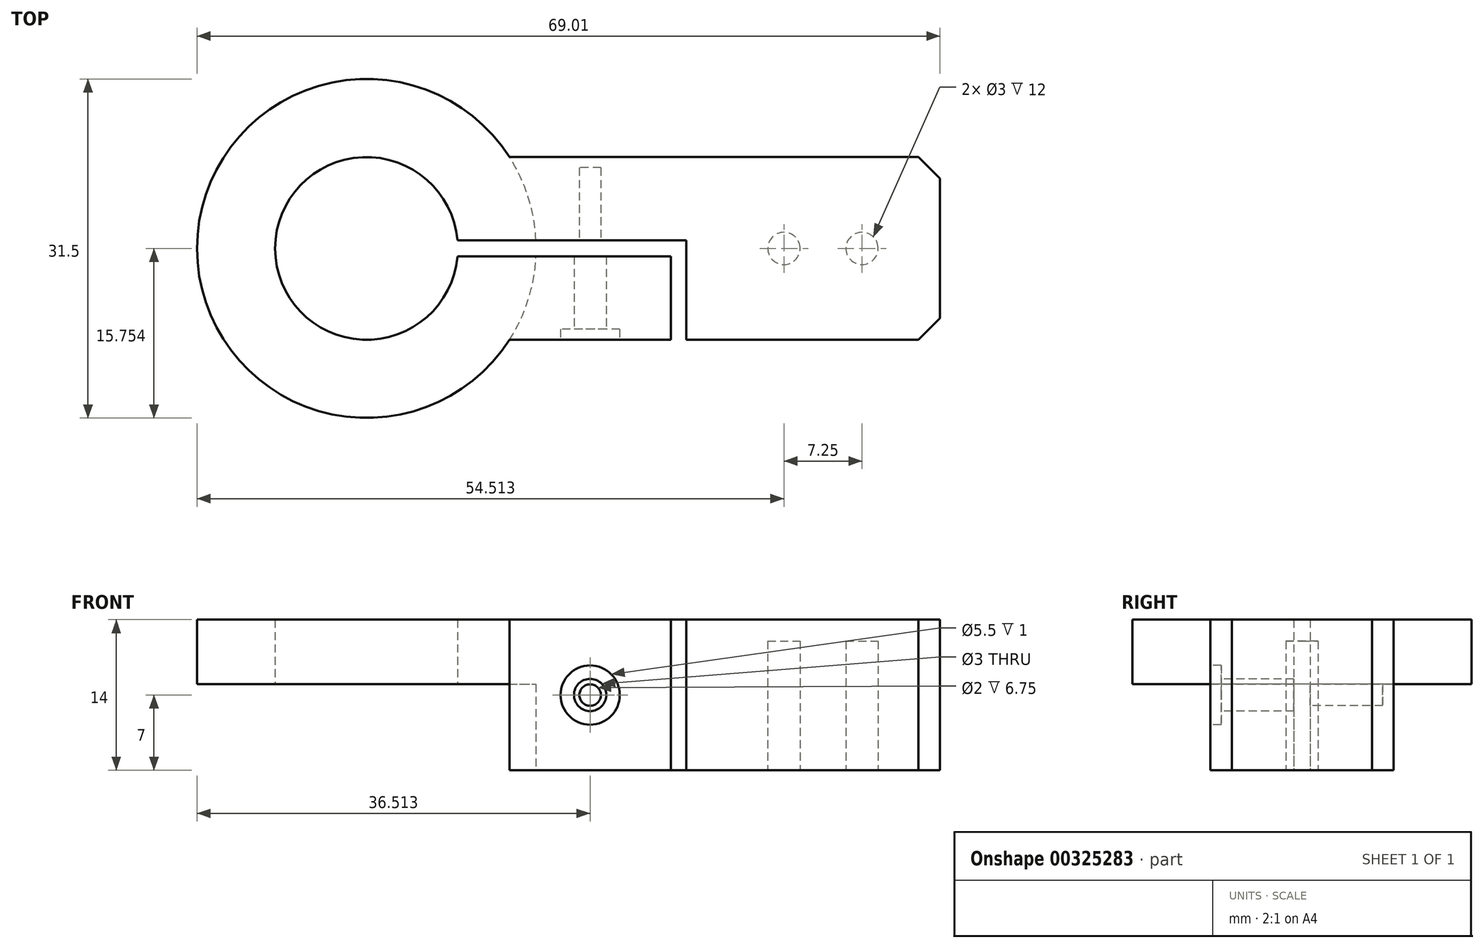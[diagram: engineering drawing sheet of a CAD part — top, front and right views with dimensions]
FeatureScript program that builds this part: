
annotation { "Feature Type Name" : "Feature", "Feature Type Description" : "" }
export const myFeature = defineFeature(function(context is Context, id is Id, definition is map)
    precondition{}
    {
        {
            var Q0;
            Q0=qCreatedBy(makeId("Top.planeOp"),FACE);
            var sketch = newSketch(context, id + "F0", { "sketchPlane" : qUnion([Q0])});
            skLineSegment(sketch, "E0.bottom", {"start": v(-112.4, -4.12) * mm, "end": v(-72.4, -4.12) * mm});
            skLineSegment(sketch, "E0.right", {"start": v(-72.4, -4.12) * mm, "end": v(-72.4, -21.12) * mm});
            skPoint(sketch, "E1", {"position": v(-141.4, -12.62) * mm});
            skArc(sketch, "E2", {"start": v(-112.4, -4.12) * mm, "mid": v(-141.4, -12.62) * mm, "end": v(-112.4, -21.12) * mm});
            skPoint(sketch, "E3", {"position": v(-134.16, -12.62) * mm});
            skPoint(sketch, "E4", {"position": v(-117.22, -13.37) * mm});
            skPoint(sketch, "E5", {"position": v(-117.22, -11.87) * mm});
            skLineSegment(sketch, "E6", {"start": v(-117.22, -13.37) * mm, "end": v(-97.4, -13.37) * mm});
            skLineSegment(sketch, "E7", {"start": v(-97.4, -13.37) * mm, "end": v(-97.4, -21.12) * mm});
            skLineSegment(sketch, "E8", {"start": v(-117.22, -11.87) * mm, "end": v(-95.97, -11.87) * mm});
            skArc(sketch, "E9", {"start": v(-117.22, -11.87) * mm, "mid": v(-134.16, -12.62) * mm, "end": v(-117.22, -13.37) * mm});
            skLineSegment(sketch, "E10", {"start": v(-95.97, -11.87) * mm, "end": v(-95.97, -21.12) * mm});
            skLineSegment(sketch, "E11", {"start": v(-95.97, -21.12) * mm, "end": v(-72.4, -21.12) * mm});
            skLineSegment(sketch, "E12", {"start": v(-112.4, -21.12) * mm, "end": v(-97.4, -21.12) * mm});
            skSolve(sketch);
        }
        {
            var Q0;
            Q0=makeQuery(id+"F0.imprint","IMPRINT",FACE,{"disambiguationData":[TD([[makeQuery(id+"F0.imprint","IMPRINT",EDGE,{"derivedFrom":sQuery(id+"F0.wireOp",EDGE,"E0.bottom")}),-1.0]])]});
            extrude(context, id + "F1", {"entities" : qUnion([Q0]), "depth" : 14 * mm});
        }
        {
            var Q0;
            Q0=makeQuery(id+"F1.opExtrude","SWEPT_FACE",FACE,{"disambiguationData":[OSD([sQuery(id+"F0.wireOp",EDGE,"E12")])]});
            var sketch = newSketch(context, id + "F2", { "sketchPlane" : qUnion([Q0])});
            skCircle(sketch, "E13", {"center": v(-104.9, 7) * mm, "radius": 2.75 * mm});
            skPoint(sketch, "E13.centerSnap0", {"position": v(-97.4, 7) * mm});
            skPoint(sketch, "E13.centerSnap1", {"position": v(-104.9, 14) * mm});
            skSolve(sketch);
        }
        {
            var Q0;
            Q0 = qSketchRegion(id + "F2", true);
            extrude(context, id + "F3", {"entities" : qUnion([Q0]), "operationType" : NewBodyOperationType.REMOVE, "oppositeDirection" : true, "depth" : 1 * mm});
        }
        {
            var Q0;
            Q0=makeQuery(id+"F3.boolean.opBoolean","COPY",FACE,{"derivedFrom":makeQuery(id+"F3.opExtrude","CAP_FACE",FACE,{"disambiguationData":[OSD([sQuery(id+"F2.wireOp",EDGE,"E13")])],"isStart":false})});
            var sketch = newSketch(context, id + "F4", { "sketchPlane" : qUnion([Q0])});
            skCircle(sketch, "E14", {"center": v(-104.9, 7) * mm, "radius": 1.5 * mm});
            skSolve(sketch);
        }
        {
            var Q0;
            Q0=makeQuery(id+"F4.imprint","IMPRINT",FACE,{"disambiguationData":[TD([[makeQuery(id+"F4.imprint","IMPRINT",EDGE,{"derivedFrom":sQuery(id+"F4.wireOp",EDGE,"E14")}),1.0]])]});
            extrude(context, id + "F5", {"entities" : qUnion([Q0]), "operationType" : NewBodyOperationType.REMOVE, "endBound" : BoundingType.UP_TO_NEXT, "oppositeDirection" : true, "depth" : 25 * mm});
        }
        {
            var Q0;
            Q0=makeQuery(id+"F3.boolean.opBoolean","COPY",FACE,{"derivedFrom":makeQuery(id+"F3.opExtrude","CAP_FACE",FACE,{"disambiguationData":[OSD([sQuery(id+"F2.wireOp",EDGE,"E13")])],"isStart":false})});
            var sketch = newSketch(context, id + "F6", { "sketchPlane" : qUnion([Q0])});
            skCircle(sketch, "E15", {"center": v(-104.9, 7) * mm, "radius": 1 * mm});
            skSolve(sketch);
        }
        {
            var Q0;
            Q0 = qSketchRegion(id + "F6", true);
            extrude(context, id + "F7", {"entities" : qUnion([Q0]), "operationType" : NewBodyOperationType.REMOVE, "oppositeDirection" : true, "depth" : 15 * mm});
        }
        {
            var Q0;
            Q0=makeQuery(id+"F1.opExtrude","CAP_FACE",FACE,{"disambiguationData":[OSD([sQuery(id+"F0.wireOp",EDGE,"E0.bottom"),sQuery(id+"F0.wireOp",EDGE,"E0.right"),sQuery(id+"F0.wireOp",EDGE,"E2"),sQuery(id+"F0.wireOp",EDGE,"E6"),sQuery(id+"F0.wireOp",EDGE,"E7"),sQuery(id+"F0.wireOp",EDGE,"E8"),sQuery(id+"F0.wireOp",EDGE,"E9"),sQuery(id+"F0.wireOp",EDGE,"E10"),sQuery(id+"F0.wireOp",EDGE,"E11"),sQuery(id+"F0.wireOp",EDGE,"E12")])],"isStart":true});
            var sketch = newSketch(context, id + "F8", { "sketchPlane" : qUnion([Q0])});
            skCircle(sketch, "E16", {"center": v(-125.67, 12.62) * mm, "radius": 15.76 * mm});
            skSolve(sketch);
        }
        {
            var Q0;
            {var subQ1=makeQuery(id+"F1.opExtrude","CAP_EDGE",EDGE,{"disambiguationData":[OSD([sQuery(id+"F0.wireOp",EDGE,"E2")])],"isStart":true});Q0=makeQuery(id+"F8.imprint","IMPRINT",FACE,{"disambiguationData":[TD([[makeQuery(id+"F8.imprint","IMPRINT",EDGE,{"derivedFrom":subQ1}),-1.0]])]});}
            extrude(context, id + "F9", {"entities" : qUnion([Q0]), "operationType" : NewBodyOperationType.REMOVE, "oppositeDirection" : true, "depth" : 8 * mm});
        }
        {
            var Q0;
            {var subQ0=sQuery(id+"F0.wireOp",EDGE,"E10");var subQ1=sQuery(id+"F0.wireOp",EDGE,"E8");var subQ2=sQuery(id+"F0.wireOp",EDGE,"E0.right");var subQ3=sQuery(id+"F0.wireOp",EDGE,"E0.bottom");var subQ4=sQuery(id+"F0.wireOp",EDGE,"E11");var subQ6=sQuery(id+"F0.wireOp",EDGE,"E2");Q0=makeQuery(id+"F9.boolean.opBoolean","SPLIT",FACE,{"disambiguationData":[TD([makeQuery(id+"F1.opExtrude","SWEPT_FACE",FACE,{"disambiguationData":[OSD([subQ3])]})])],"derivedFrom":makeQuery(id+"F1.opExtrude","CAP_FACE",FACE,{"disambiguationData":[OSD([subQ3,subQ2,subQ6,sQuery(id+"F0.wireOp",EDGE,"E6"),sQuery(id+"F0.wireOp",EDGE,"E7"),subQ1,sQuery(id+"F0.wireOp",EDGE,"E9"),subQ0,subQ4,sQuery(id+"F0.wireOp",EDGE,"E12")])],"isStart":true})});}
            var sketch = newSketch(context, id + "F10", { "sketchPlane" : qUnion([Q0])});
            skPoint(sketch, "E17", {"position": v(-79.65, 12.62) * mm});
            skPoint(sketch, "E18", {"position": v(-86.9, 12.62) * mm});
            skCircle(sketch, "E19", {"center": v(-79.65, 12.62) * mm, "radius": 1.5 * mm});
            skCircle(sketch, "E20", {"center": v(-86.9, 12.62) * mm, "radius": 1.5 * mm});
            skSolve(sketch);
        }
        {
            var Q0;
            Q0=makeQuery(id+"F10.imprint","IMPRINT",FACE,{"disambiguationData":[TD([[makeQuery(id+"F10.imprint","IMPRINT",EDGE,{"derivedFrom":sQuery(id+"F10.wireOp",EDGE,"E19")}),1.0]])]});
            var Q1;
            Q1=makeQuery(id+"F10.imprint","IMPRINT",FACE,{"disambiguationData":[TD([[makeQuery(id+"F10.imprint","IMPRINT",EDGE,{"derivedFrom":sQuery(id+"F10.wireOp",EDGE,"E20")}),1.0]])]});
            extrude(context, id + "F11", {"entities" : qUnion([Q0, Q1]), "operationType" : NewBodyOperationType.REMOVE, "oppositeDirection" : true, "depth" : 12 * mm});
        }
        {
            var Q0;
            Q0=makeQuery(id+"F1.opExtrude","SWEPT_EDGE",EDGE,{"disambiguationData":[OSD([sQuery(id+"F0.wireOp",EDGE,"E0.bottom"),sQuery(id+"F0.wireOp",EDGE,"E0.right")])]});
            var Q1;
            Q1=makeQuery(id+"F1.opExtrude","SWEPT_EDGE",EDGE,{"disambiguationData":[OSD([sQuery(id+"F0.wireOp",EDGE,"E0.right"),sQuery(id+"F0.wireOp",EDGE,"E11")])]});
            chamfer(context, id + "F12", {"entities" : qUnion([Q0, Q1]), "width" : 2 * mm, "tangentPropagation" : true});
        }
    });
